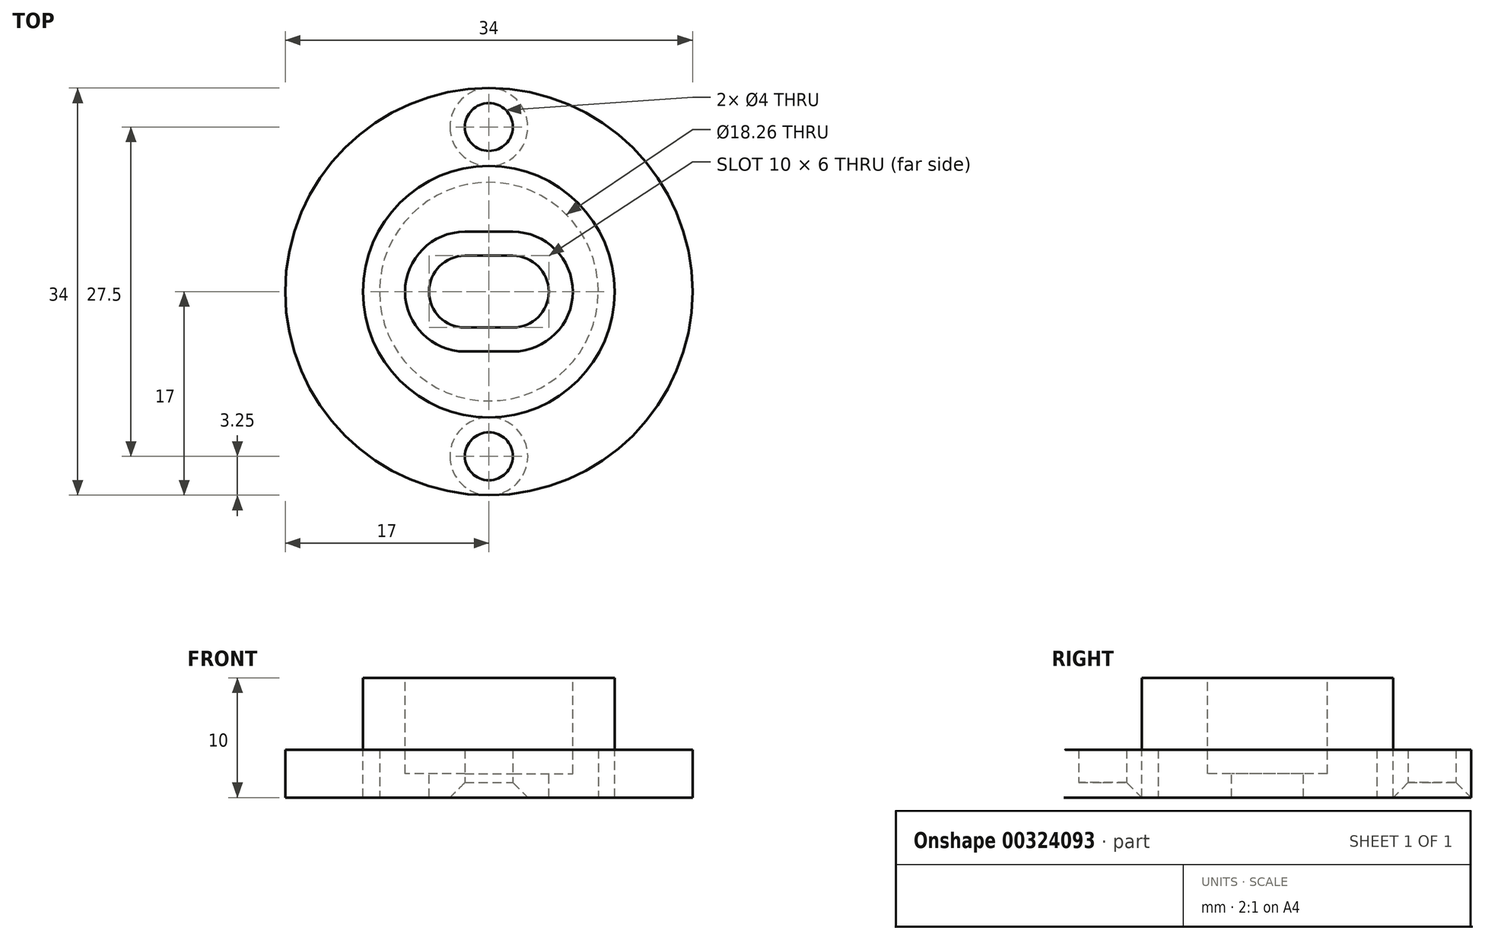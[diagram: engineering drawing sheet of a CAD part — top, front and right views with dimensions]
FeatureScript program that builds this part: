
annotation { "Feature Type Name" : "Feature", "Feature Type Description" : "" }
export const myFeature = defineFeature(function(context is Context, id is Id, definition is map)
    precondition{}
    {
        {
            var Q0;
            Q0=qCreatedBy(makeId("Top.planeOp"),FACE);
            var sketch = newSketch(context, id + "F0", { "sketchPlane" : qUnion([Q0])});
            skCircle(sketch, "E0", {"center": v(0, 0) * mm, "radius": 10.5 * mm});
            skLineSegment(sketch, "E1.bottom", {"start": v(-2, 3) * mm, "end": v(2, 3) * mm});
            skLineSegment(sketch, "E1.top", {"start": v(-2, -3) * mm, "end": v(2, -3) * mm});
            skLineSegment(sketch, "E1.left", {"start": v(-5, 0) * mm, "end": v(-5, 0) * mm});
            skLineSegment(sketch, "E1.right", {"start": v(5, 0) * mm, "end": v(5, 0) * mm});
            skPoint(sketch, "E2.visualSharp", {"position": v(-5, 3) * mm});
            skArc(sketch, "E2.filletArc", {"start": v(-2, 3) * mm, "mid": v(-4.12, 2.12) * mm, "end": v(-5, 0) * mm});
            skPoint(sketch, "E3.visualSharp", {"position": v(-5, -3) * mm});
            skArc(sketch, "E3.filletArc", {"start": v(-5, 0) * mm, "mid": v(-4.12, -2.12) * mm, "end": v(-2, -3) * mm});
            skPoint(sketch, "E4.visualSharp", {"position": v(5, -3) * mm});
            skArc(sketch, "E4.filletArc", {"start": v(2, -3) * mm, "mid": v(4.12, -2.12) * mm, "end": v(5, 0) * mm});
            skPoint(sketch, "E5.visualSharp", {"position": v(5, 3) * mm});
            skArc(sketch, "E5.filletArc", {"start": v(5, 0) * mm, "mid": v(4.12, 2.12) * mm, "end": v(2, 3) * mm});
            skSolve(sketch);
        }
        {
            var Q0;
            Q0=makeQuery(id+"F0.imprint","IMPRINT",FACE,{"disambiguationData":[TD([[makeQuery(id+"F0.imprint","IMPRINT",EDGE,{"derivedFrom":sQuery(id+"F0.wireOp",EDGE,"E0")}),1.0]])]});
            extrude(context, id + "F1", {"entities" : qUnion([Q0]), "oppositeDirection" : true, "offsetDistance" : 25 * mm, "depth" : 10 * mm});
        }
        {
            var Q0;
            Q0=makeQuery(id+"F1.opExtrude","CAP_FACE",FACE,{"disambiguationData":[OSD([sQuery(id+"F0.wireOp",EDGE,"E0"),sQuery(id+"F0.wireOp",EDGE,"E1.bottom"),sQuery(id+"F0.wireOp",EDGE,"E1.top"),sQuery(id+"F0.wireOp",EDGE,"E1.left"),sQuery(id+"F0.wireOp",EDGE,"E1.right")])],"isStart":false});
            cPlane(context, id + "F2", {"entities" : qUnion([Q0]), "cplaneType" : CPlaneType.OFFSET, "offset" : 0 * mm, "width" : 150 * mm, "height" : 150 * mm});
        }
        {
            var Q0;
            Q0=qCreatedBy(id+"F2.planeOp",FACE);
            var sketch = newSketch(context, id + "F3", { "sketchPlane" : qUnion([Q0])});
            skCircle(sketch, "E6", {"center": v(0, 0) * mm, "radius": 17 * mm});
            skCircle(sketch, "E7", {"center": v(0, 0) * mm, "radius": 13.75 * mm, "construction": true});
            skCircle(sketch, "E8", {"center": v(0, 0) * mm, "radius": 9.13 * mm});
            skCircle(sketch, "E9", {"center": v(0, 13.75) * mm, "radius": 2 * mm});
            skCircle(sketch, "E10", {"center": v(0, -13.75) * mm, "radius": 2 * mm});
            skSolve(sketch);
        }
        {
            var Q0;
            Q0 = qSketchRegion(id + "F3", true);
            extrude(context, id + "F4", {"entities" : qUnion([Q0]), "oppositeDirection" : true, "depth" : 4 * mm, "offsetDistance" : 25 * mm});
        }
        {
            var Q0;
            Q0=sQuery(id+"F3.wireOp",VERTEX,"E9.center");
            var Q1;
            Q1=sQuery(id+"F3.wireOp",VERTEX,"E10.center");
            var Q2;
            Q2=makeQuery(id+"F4.opExtrude","SWEPT_BODY",BODY,{"disambiguationData":[OSD([sQuery(id+"F3.wireOp",EDGE,"E6"),sQuery(id+"F3.wireOp",EDGE,"E8"),sQuery(id+"F3.wireOp",EDGE,"E9"),sQuery(id+"F3.wireOp",EDGE,"E10")])]});
            hole(context, id + "F5", {"style" : HoleStyle.C_SINK, "endStyle" : HoleEndStyle.BLIND, "holeDiameter" : 4 * mm, "cSinkDiameter" : 6.5 * mm, "cSinkAngle" : 90 * degree, "holeDepth" : 10 * mm, "tappedDepth" : 12 * mm, "tapClearance" : 3, "locations" : qUnion([Q0, Q1]), "scope" : qUnion([Q2])});
        }
        {
            var Q0;
            Q0=makeQuery(id+"F1.opExtrude","CAP_FACE",FACE,{"disambiguationData":[OSD([sQuery(id+"F0.wireOp",EDGE,"E0"),sQuery(id+"F0.wireOp",EDGE,"E1.bottom"),sQuery(id+"F0.wireOp",EDGE,"E1.top"),sQuery(id+"F0.wireOp",EDGE,"E2.filletArc"),sQuery(id+"F0.wireOp",EDGE,"E3.filletArc"),sQuery(id+"F0.wireOp",EDGE,"E4.filletArc"),sQuery(id+"F0.wireOp",EDGE,"E5.filletArc")])],"isStart":true});
            var sketch = newSketch(context, id + "F6", { "sketchPlane" : qUnion([Q0])});
            skLineSegment(sketch, "E11.bottom", {"start": v(-2, 5) * mm, "end": v(2, 5) * mm});
            skLineSegment(sketch, "E11.top", {"start": v(-2, -5) * mm, "end": v(2, -5) * mm});
            skLineSegment(sketch, "E11.left", {"start": v(-7, 0) * mm, "end": v(-7, 0) * mm});
            skLineSegment(sketch, "E11.right", {"start": v(7, 0) * mm, "end": v(7, 0) * mm});
            skPoint(sketch, "E11.middle", {"position": v(0, 0) * mm});
            skPoint(sketch, "E12.visualSharp", {"position": v(-7, 5) * mm});
            skArc(sketch, "E12.filletArc", {"start": v(-2, 5) * mm, "mid": v(-5.54, 3.54) * mm, "end": v(-7, 0) * mm});
            skPoint(sketch, "E13.visualSharp", {"position": v(-7, -5) * mm});
            skArc(sketch, "E13.filletArc", {"start": v(-7, 0) * mm, "mid": v(-5.54, -3.54) * mm, "end": v(-2, -5) * mm});
            skPoint(sketch, "E14.visualSharp", {"position": v(7, -5) * mm});
            skArc(sketch, "E14.filletArc", {"start": v(2, -5) * mm, "mid": v(5.54, -3.54) * mm, "end": v(7, 0) * mm});
            skPoint(sketch, "E15.visualSharp", {"position": v(7, 5) * mm});
            skArc(sketch, "E15.filletArc", {"start": v(7, 0) * mm, "mid": v(5.54, 3.54) * mm, "end": v(2, 5) * mm});
            skSolve(sketch);
        }
        {
            var Q0;
            Q0=makeQuery(id+"F6.imprint","IMPRINT",FACE,{"disambiguationData":[TD([[makeQuery(id+"F6.imprint","IMPRINT",EDGE,{"derivedFrom":sQuery(id+"F6.wireOp",EDGE,"E11.bottom")}),-1.0]])]});
            extrude(context, id + "F7", {"entities" : qUnion([Q0]), "operationType" : NewBodyOperationType.REMOVE, "oppositeDirection" : true, "depth" : 8 * mm, "offsetDistance" : 25 * mm});
        }
    });
